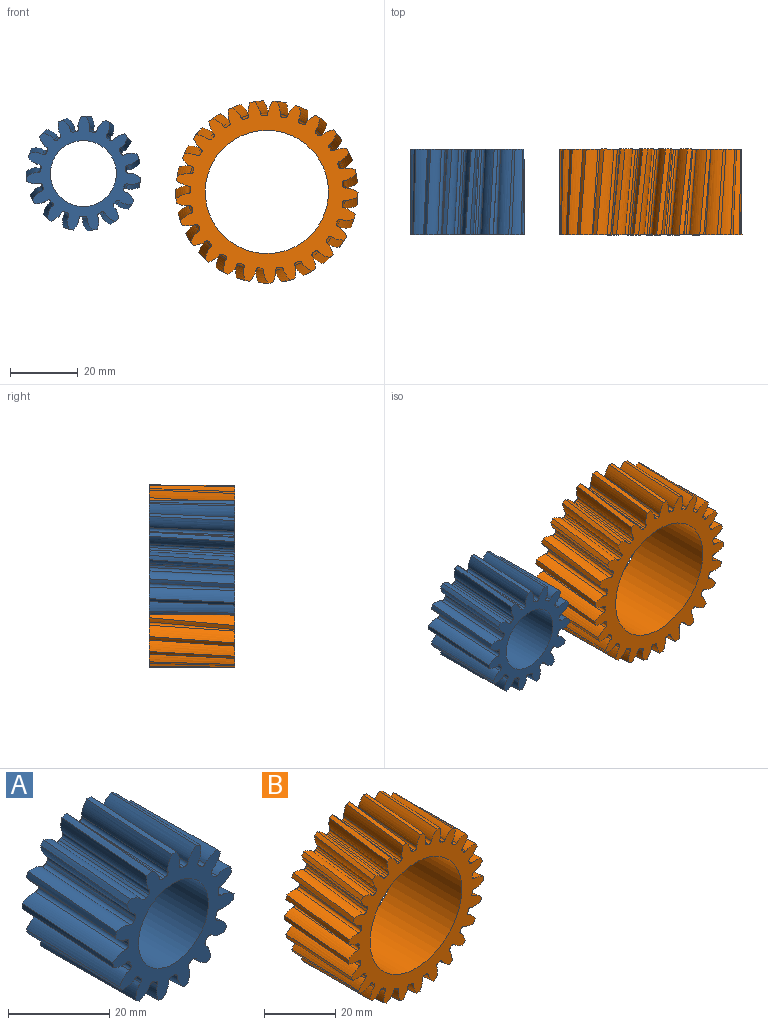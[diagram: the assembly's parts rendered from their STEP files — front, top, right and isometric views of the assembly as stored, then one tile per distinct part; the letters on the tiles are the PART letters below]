
ASSEMBLY  parts=2 mates=1
PART A: 93 faces, bbox 34.1x40.7x34 mm
  f0: bspline ~40.64x3.67mm, area 33.3mm2, adj f1,f89,f90,f91
  f1: bspline ~40.64x4.83mm, area 99.2mm2, adj f0,f2,f90,f91
  f2: bspline ~40.64x2.21mm, area 31.7mm2, adj f1,f3,f90,f91
  f3: bspline ~40.64x2.21mm, area 18mm2, adj f2,f4,f90,f91
  f4: bspline ~40.64x2.73mm, area 31.7mm2, adj f3,f5,f90,f91
  f5: bspline ~40.64x5.08mm, area 99.2mm2, adj f4,f6,f90,f91
  f6: bspline ~40.64x2.88mm, area 33.3mm2, adj f5,f7,f90,f91
  f7: bspline ~40.64x5.06mm, area 99.2mm2, adj f6,f8,f90,f91
  f8: bspline ~40.64x2.78mm, area 31.7mm2, adj f7,f9,f90,f91
  f9: bspline ~40.64x2.29mm, area 18mm2, adj f8,f10,f90,f91
  f10: bspline ~40.64x2.3mm, area 31.7mm2, adj f9,f11,f90,f91
  f11: bspline ~40.64x4.74mm, area 99.2mm2, adj f10,f12,f90,f91
  f12: bspline ~40.64x3.74mm, area 33.3mm2, adj f11,f13,f90,f91
  f13: bspline ~40.64x4.41mm, area 99.2mm2, adj f12,f14,f90,f91
  f14: bspline ~40.64x2.94mm, area 31.7mm2, adj f13,f15,f90,f91
  f15: bspline ~40.64x2.66mm, area 18mm2, adj f14,f16,f90,f91
  f16: bspline ~40.64x2.77mm, area 31.7mm2, adj f15,f17,f90,f91
  f17: bspline ~40.64x3.73mm, area 99.2mm2, adj f16,f18,f90,f91
  f18: bspline ~40.64x3.96mm, area 33.3mm2, adj f17,f19,f90,f91
  f19: bspline ~40.64x4.1mm, area 99.2mm2, adj f18,f20,f90,f91
  f20: bspline ~40.64x2.64mm, area 31.7mm2, adj f19,f21,f90,f91
  f21: bspline ~40.64x2.57mm, area 18mm2, adj f20,f22,f90,f91
  f22: bspline ~40.64x2.94mm, area 31.7mm2, adj f21,f23,f90,f91
  f23: bspline ~40.64x4.75mm, area 99.2mm2, adj f22,f24,f90,f91
  f24: bspline ~40.64x3.49mm, area 33.3mm2, adj f23,f25,f90,f91
  f25: bspline ~40.64x4.97mm, area 99.2mm2, adj f24,f26,f90,f91
  f26: bspline ~40.64x2.35mm, area 31.7mm2, adj f25,f27,f90,f91
  f27: bspline ~40.64x2.04mm, area 18mm2, adj f26,f28,f90,f91
  f28: bspline ~40.64x2.6mm, area 31.7mm2, adj f27,f29,f90,f91
  f29: bspline ~40.64x5.07mm, area 99.2mm2, adj f28,f30,f90,f91
  f30: bspline ~25.4x2.31mm, area 33.3mm2, adj f29,f31,f90,f91
  f31: bspline ~40.64x4.98mm, area 99.2mm2, adj f30,f32,f90,f91
  f32: bspline ~40.64x2.87mm, area 31.7mm2, adj f31,f33,f90,f91
  f33: bspline ~40.64x2.42mm, area 18mm2, adj f32,f34,f90,f91
  f34: bspline ~40.64x2.45mm, area 31.7mm2, adj f33,f35,f90,f91
  f35: bspline ~40.64x4.52mm, area 99.2mm2, adj f34,f36,f90,f91
  f36: bspline ~40.64x3.86mm, area 33.3mm2, adj f35,f37,f90,f91
  f37: bspline ~40.64x4.13mm, area 99.2mm2, adj f36,f38,f90,f91
  f38: bspline ~40.64x2.89mm, area 31.7mm2, adj f37,f39,f90,f91
  f39: bspline ~40.64x2.68mm, area 18mm2, adj f38,f40,f90,f91
  f40: bspline ~40.64x2.86mm, area 31.7mm2, adj f39,f41,f90,f91
  f41: bspline ~40.64x3.98mm, area 99.2mm2, adj f40,f42,f90,f91
  f42: bspline ~40.64x3.91mm, area 33.3mm2, adj f41,f43,f90,f91
  f43: bspline ~40.64x4.39mm, area 99.2mm2, adj f42,f44,f90,f91
  f44: bspline ~40.64x2.52mm, area 31.7mm2, adj f43,f45,f90,f91
  f45: bspline ~40.64x2.48mm, area 18mm2, adj f44,f46,f90,f91
  f46: bspline ~40.64x2.9mm, area 31.7mm2, adj f45,f47,f90,f91
  f47: bspline ~40.64x4.92mm, area 99.2mm2, adj f46,f48,f90,f91
  f48: bspline ~40.64x3.27mm, area 33.3mm2, adj f47,f49,f90,f91
  f49: bspline ~40.64x5.05mm, area 99.2mm2, adj f48,f50,f90,f91
  f50: bspline ~40.64x2.52mm, area 31.7mm2, adj f49,f51,f90,f91
  f51: bspline ~40.64x1.95mm, area 18mm2, adj f50,f52,f90,f91
  f52: bspline ~40.64x2.44mm, area 31.7mm2, adj f51,f53,f90,f91
  f53: bspline ~40.64x5.02mm, area 99.2mm2, adj f52,f54,f90,f91
  f54: bspline ~40.64x3.39mm, area 33.3mm2, adj f53,f55,f90,f91
  f55: bspline ~40.64x4.84mm, area 99.2mm2, adj f54,f56,f90,f91
  f56: bspline ~40.64x2.92mm, area 31.7mm2, adj f55,f57,f90,f91
  f57: bspline ~40.64x2.53mm, area 18mm2, adj f56,f58,f90,f91
  f58: bspline ~40.64x2.58mm, area 31.7mm2, adj f57,f59,f90,f91
  f59: bspline ~40.64x4.25mm, area 99.2mm2, adj f58,f60,f90,f91
  f60: bspline ~40.64x3.94mm, area 33.3mm2, adj f59,f61,f90,f91
  f61: bspline ~40.64x3.84mm, area 99.2mm2, adj f60,f62,f90,f91
  f62: bspline ~40.64x2.82mm, area 31.7mm2, adj f61,f63,f90,f91
  f63: bspline ~40.64x2.67mm, area 18mm2, adj f62,f64,f90,f91
  f64: bspline ~40.64x2.92mm, area 31.7mm2, adj f63,f65,f90,f91
  f65: bspline ~40.64x4.28mm, area 99.2mm2, adj f64,f66,f90,f91
  f66: bspline ~40.64x3.81mm, area 33.3mm2, adj f65,f67,f90,f91
  f67: bspline ~40.64x4.63mm, area 99.2mm2, adj f66,f68,f90,f91
  f68: bspline ~40.64x2.38mm, area 31.7mm2, adj f67,f69,f90,f91
  f69: bspline ~40.64x2.36mm, area 18mm2, adj f68,f70,f90,f91
  f70: bspline ~40.64x2.83mm, area 31.7mm2, adj f69,f71,f90,f91
  f71: bspline ~40.64x5.02mm, area 99.2mm2, adj f70,f72,f90,f91
  f72: bspline ~40.64x3.02mm, area 33.3mm2, adj f71,f73,f90,f91
  f73: bspline ~40.64x5.08mm, area 99.2mm2, adj f72,f74,f90,f91
  f74: bspline ~40.64x2.67mm, area 31.7mm2, adj f73,f75,f90,f91
  f75: bspline ~40.64x2.13mm, area 18mm2, adj f74,f76,f90,f91
  f76: bspline ~40.64x2.25mm, area 31.7mm2, adj f75,f77,f90,f91
  f77: bspline ~40.64x4.9mm, area 99.2mm2, adj f76,f78,f90,f91
  f78: bspline ~40.64x3.58mm, area 33.3mm2, adj f77,f79,f90,f91
  f79: bspline ~40.64x4.65mm, area 99.2mm2, adj f78,f80,f90,f91
  f80: bspline ~40.64x2.95mm, area 31.7mm2, adj f79,f81,f90,f91
  f81: bspline ~40.64x2.61mm, area 18mm2, adj f80,f82,f90,f91
  f82: bspline ~40.64x2.68mm, area 31.7mm2, adj f81,f83,f90,f91
  f83: bspline ~40.64x3.95mm, area 99.2mm2, adj f82,f84,f90,f91
  f84: bspline ~40.64x3.97mm, area 33.3mm2, adj f83,f85,f90,f91
  f85: bspline ~40.64x3.85mm, area 99.2mm2, adj f84,f86,f90,f91
  f86: bspline ~40.64x2.72mm, area 31.7mm2, adj f85,f87,f90,f91
  f87: bspline ~40.64x2.64mm, area 18mm2, adj f86,f88,f90,f91
  f88: bspline ~40.64x2.95mm, area 31.7mm2, adj f87,f89,f90,f91
  f89: bspline ~40.64x4.54mm, area 99.2mm2, adj f0,f88,f90,f91
  f90: plane 33.95x33.78mm, normal (0,1,0), area 389.3mm2, adj f0,f1,f2,f3,f4,f5,f6,f7
  f91: plane 33.95x33.8mm, normal (0,-1,0), area 389.7mm2, adj f0,f1,f2,f3,f4,f5,f6,f7
  f92: cylinder r=9.78mm len=25.4mm, axis (0,-1,0), area 1560.7mm2, adj f90,f91
PART B: 153 faces, bbox 54.1x40.7x54.1 mm
  f0: bspline ~40.64x4.19mm, area 36.5mm2, adj f1,f149,f150,f151
  f1: bspline ~40.64x6.35mm, area 99.8mm2, adj f0,f2,f150,f151
  f2: bspline ~40.64x3.93mm, area 29.9mm2, adj f1,f3,f150,f151
  f3: bspline ~40.64x3.45mm, area 17.2mm2, adj f2,f4,f150,f151
  f4: bspline ~40.64x3.43mm, area 29.9mm2, adj f3,f5,f150,f151
  f5: bspline ~40.64x5.8mm, area 99.8mm2, adj f4,f6,f150,f151
  f6: bspline ~40.64x5.01mm, area 36.5mm2, adj f5,f7,f150,f151
  f7: bspline ~40.64x6.28mm, area 99.8mm2, adj f6,f8,f150,f151
  f8: bspline ~40.64x4.31mm, area 29.9mm2, adj f7,f9,f150,f151
  f9: bspline ~40.64x3.95mm, area 17.2mm2, adj f8,f10,f150,f151
  f10: bspline ~40.64x3.98mm, area 29.9mm2, adj f9,f11,f150,f151
  f11: bspline ~40.64x4.97mm, area 99.8mm2, adj f10,f12,f150,f151
  f12: bspline ~40.64x5.51mm, area 36.5mm2, adj f11,f13,f150,f151
  f13: bspline ~40.64x5.81mm, area 99.8mm2, adj f12,f14,f150,f151
  f14: bspline ~40.64x4.42mm, area 29.9mm2, adj f13,f15,f150,f151
  f15: bspline ~40.64x4.2mm, area 17.2mm2, adj f14,f16,f150,f151
  f16: bspline ~40.64x4.29mm, area 29.9mm2, adj f15,f17,f150,f151
  f17: bspline ~40.64x5.13mm, area 99.8mm2, adj f16,f18,f150,f151
  f18: bspline ~40.64x5.67mm, area 36.5mm2, adj f17,f19,f150,f151
  f19: bspline ~40.64x5.02mm, area 99.8mm2, adj f18,f20,f150,f151
  f20: bspline ~40.64x4.25mm, area 29.9mm2, adj f19,f21,f150,f151
  f21: bspline ~40.64x4.18mm, area 17.2mm2, adj f20,f22,f150,f151
  f22: bspline ~40.64x4.42mm, area 29.9mm2, adj f21,f23,f150,f151
  f23: bspline ~40.64x5.89mm, area 99.8mm2, adj f22,f24,f150,f151
  f24: bspline ~40.64x5.47mm, area 36.5mm2, adj f23,f25,f150,f151
  f25: bspline ~40.64x5.09mm, area 99.8mm2, adj f24,f26,f150,f151
  f26: bspline ~40.64x3.92mm, area 29.9mm2, adj f25,f27,f150,f151
  f27: bspline ~40.64x3.9mm, area 17.2mm2, adj f26,f28,f150,f151
  f28: bspline ~40.64x4.28mm, area 29.9mm2, adj f27,f29,f150,f151
  f29: bspline ~40.64x6.31mm, area 99.8mm2, adj f28,f30,f150,f151
  f30: bspline ~40.64x4.92mm, area 36.5mm2, adj f29,f31,f150,f151
  f31: bspline ~40.64x5.88mm, area 99.8mm2, adj f30,f32,f150,f151
  f32: bspline ~40.64x3.35mm, area 29.9mm2, adj f31,f33,f150,f151
  f33: bspline ~40.64x3.38mm, area 17.2mm2, adj f32,f34,f150,f151
  f34: bspline ~40.64x3.87mm, area 29.9mm2, adj f33,f35,f150,f151
  f35: bspline ~40.64x6.33mm, area 99.8mm2, adj f34,f36,f150,f151
  f36: bspline ~40.64x4.07mm, area 36.5mm2, adj f35,f37,f150,f151
  f37: bspline ~40.64x6.3mm, area 99.8mm2, adj f36,f38,f150,f151
  f38: bspline ~40.64x3.8mm, area 29.9mm2, adj f37,f39,f150,f151
  f39: bspline ~40.64x3.3mm, area 17.2mm2, adj f38,f40,f150,f151
  f40: bspline ~40.64x3.26mm, area 29.9mm2, adj f39,f41,f150,f151
  f41: bspline ~40.64x5.96mm, area 99.8mm2, adj f40,f42,f150,f151
  f42: bspline ~40.64x4.83mm, area 36.5mm2, adj f41,f43,f150,f151
  f43: bspline ~40.64x6.33mm, area 99.8mm2, adj f42,f44,f150,f151
  f44: bspline ~40.64x4.24mm, area 29.9mm2, adj f43,f45,f150,f151
  f45: bspline ~40.64x3.85mm, area 17.2mm2, adj f44,f46,f150,f151
  f46: bspline ~40.64x3.87mm, area 29.9mm2, adj f45,f47,f150,f151
  f47: bspline ~40.64x5.21mm, area 99.8mm2, adj f46,f48,f150,f151
  f48: bspline ~40.64x5.42mm, area 36.5mm2, adj f47,f49,f150,f151
  f49: bspline ~40.64x5.96mm, area 99.8mm2, adj f48,f50,f150,f151
  f50: bspline ~40.64x4.42mm, area 29.9mm2, adj f49,f51,f150,f151
  f51: bspline ~40.64x4.16mm, area 17.2mm2, adj f50,f52,f150,f151
  f52: bspline ~40.64x4.23mm, area 29.9mm2, adj f51,f53,f150,f151
  f53: bspline ~40.64x4.91mm, area 99.8mm2, adj f52,f54,f150,f151
  f54: bspline ~40.64x5.66mm, area 36.5mm2, adj f53,f55,f150,f151
  f55: bspline ~40.64x5.23mm, area 99.8mm2, adj f54,f56,f150,f151
  f56: bspline ~40.64x4.32mm, area 29.9mm2, adj f55,f57,f150,f151
  f57: bspline ~40.64x4.21mm, area 17.2mm2, adj f56,f58,f150,f151
  f58: bspline ~40.64x4.41mm, area 29.9mm2, adj f57,f59,f150,f151
  f59: bspline ~40.64x5.72mm, area 99.8mm2, adj f58,f60,f150,f151
  f60: bspline ~40.64x5.55mm, area 36.5mm2, adj f59,f61,f150,f151
  f61: bspline ~40.64x4.84mm, area 99.8mm2, adj f60,f62,f150,f151
  f62: bspline ~40.64x4.03mm, area 29.9mm2, adj f61,f63,f150,f151
  f63: bspline ~40.64x3.99mm, area 17.2mm2, adj f62,f64,f150,f151
  f64: bspline ~40.64x4.34mm, area 29.9mm2, adj f63,f65,f150,f151
  f65: bspline ~40.64x6.24mm, area 99.8mm2, adj f64,f66,f150,f151
  f66: bspline ~40.64x5.09mm, area 36.5mm2, adj f65,f67,f150,f151
  f67: bspline ~40.64x5.72mm, area 99.8mm2, adj f66,f68,f150,f151
  f68: bspline ~40.64x3.51mm, area 29.9mm2, adj f67,f69,f150,f151
  f69: bspline ~40.64x3.53mm, area 17.2mm2, adj f68,f70,f150,f151
  f70: bspline ~40.64x3.99mm, area 29.9mm2, adj f69,f71,f150,f151
  f71: bspline ~40.64x6.36mm, area 99.8mm2, adj f70,f72,f150,f151
  f72: bspline ~40.64x4.31mm, area 36.5mm2, adj f71,f73,f150,f151
  f73: bspline ~40.64x6.24mm, area 99.8mm2, adj f72,f74,f150,f151
  f74: bspline ~40.64x3.65mm, area 29.9mm2, adj f73,f75,f150,f151
  f75: bspline ~40.64x3.12mm, area 17.2mm2, adj f74,f76,f150,f151
  f76: bspline ~40.64x3.4mm, area 29.9mm2, adj f75,f77,f150,f151
  f77: bspline ~40.64x6.09mm, area 99.8mm2, adj f76,f78,f150,f151
  f78: bspline ~40.64x4.64mm, area 36.5mm2, adj f77,f79,f150,f151
  f79: bspline ~40.64x6.36mm, area 99.8mm2, adj f78,f80,f150,f151
  f80: bspline ~40.64x4.16mm, area 29.9mm2, adj f79,f81,f150,f151
  f81: bspline ~40.64x3.73mm, area 17.2mm2, adj f80,f82,f150,f151
  f82: bspline ~40.64x3.74mm, area 29.9mm2, adj f81,f83,f150,f151
  f83: bspline ~40.64x5.43mm, area 99.8mm2, adj f82,f84,f150,f151
  f84: bspline ~40.64x5.3mm, area 36.5mm2, adj f83,f85,f150,f151
  f85: bspline ~40.64x6.09mm, area 99.8mm2, adj f84,f86,f150,f151
  f86: bspline ~40.64x4.4mm, area 29.9mm2, adj f85,f87,f150,f151
  f87: bspline ~40.64x4.11mm, area 17.2mm2, adj f86,f88,f150,f151
  f88: bspline ~40.64x4.16mm, area 29.9mm2, adj f87,f89,f150,f151
  f89: bspline ~40.64x4.69mm, area 99.8mm2, adj f88,f90,f150,f151
  f90: bspline ~40.64x5.63mm, area 36.5mm2, adj f89,f91,f150,f151
  f91: bspline ~40.64x5.44mm, area 99.8mm2, adj f90,f92,f150,f151
  f92: bspline ~40.64x4.37mm, area 29.9mm2, adj f91,f93,f150,f151
  f93: bspline ~40.64x4.22mm, area 17.2mm2, adj f92,f94,f150,f151
  f94: bspline ~40.64x4.39mm, area 29.9mm2, adj f93,f95,f150,f151
  f95: bspline ~40.64x5.54mm, area 99.8mm2, adj f94,f96,f150,f151
  f96: bspline ~40.64x5.61mm, area 36.5mm2, adj f95,f97,f150,f151
  f97: bspline ~40.64x4.58mm, area 99.8mm2, adj f96,f98,f150,f151
  f98: bspline ~40.64x4.12mm, area 29.9mm2, adj f97,f99,f150,f151
  f99: bspline ~40.64x4.07mm, area 17.2mm2, adj f98,f100,f150,f151
  f100: bspline ~40.64x4.38mm, area 29.9mm2, adj f99,f101,f150,f151
  f101: bspline ~40.64x6.15mm, area 99.8mm2, adj f100,f102,f150,f151
  f102: bspline ~40.64x5.24mm, area 36.5mm2, adj f101,f103,f150,f151
  f103: bspline ~40.64x5.53mm, area 99.8mm2, adj f102,f104,f150,f151
  f104: bspline ~40.64x3.67mm, area 29.9mm2, adj f103,f105,f150,f151
  f105: bspline ~40.64x3.67mm, area 17.2mm2, adj f104,f106,f150,f151
  f106: bspline ~40.64x4.11mm, area 29.9mm2, adj f105,f107,f150,f151
  f107: bspline ~40.64x6.37mm, area 99.8mm2, adj f106,f108,f150,f151
  f108: bspline ~40.64x4.53mm, area 36.5mm2, adj f107,f109,f150,f151
  f109: bspline ~40.64x6.14mm, area 99.8mm2, adj f108,f110,f150,f151
  f110: bspline ~40.64x3.49mm, area 29.9mm2, adj f109,f111,f150,f151
  f111: bspline ~40.64x3.03mm, area 17.2mm2, adj f110,f112,f150,f151
  f112: bspline ~40.64x3.57mm, area 29.9mm2, adj f111,f113,f150,f151
  f113: bspline ~40.64x6.19mm, area 99.8mm2, adj f112,f114,f150,f151
  f114: bspline ~40.64x4.42mm, area 36.5mm2, adj f113,f115,f150,f151
  f115: bspline ~40.64x6.37mm, area 99.8mm2, adj f114,f116,f150,f151
  f116: bspline ~40.64x4.05mm, area 29.9mm2, adj f115,f117,f150,f151
  f117: bspline ~40.64x3.6mm, area 17.2mm2, adj f116,f118,f150,f151
  f118: bspline ~40.64x3.59mm, area 29.9mm2, adj f117,f119,f150,f151
  f119: bspline ~40.64x5.63mm, area 99.8mm2, adj f118,f120,f150,f151
  f120: bspline ~40.64x5.17mm, area 36.5mm2, adj f119,f121,f150,f151
  f121: bspline ~40.64x6.2mm, area 99.8mm2, adj f120,f122,f150,f151
  f122: bspline ~40.64x4.36mm, area 29.9mm2, adj f121,f123,f150,f151
  f123: bspline ~40.64x4.04mm, area 17.2mm2, adj f122,f124,f150,f151
  f124: bspline ~40.64x4.08mm, area 29.9mm2, adj f123,f125,f150,f151
  f125: bspline ~40.64x4.71mm, area 99.8mm2, adj f124,f126,f150,f151
  f126: bspline ~40.64x5.58mm, area 36.5mm2, adj f125,f127,f150,f151
  f127: bspline ~40.64x5.63mm, area 99.8mm2, adj f126,f128,f150,f151
  f128: bspline ~40.64x4.4mm, area 29.9mm2, adj f127,f129,f150,f151
  f129: bspline ~40.64x4.22mm, area 17.2mm2, adj f128,f130,f150,f151
  f130: bspline ~40.64x4.35mm, area 29.9mm2, adj f129,f131,f150,f151
  f131: bspline ~40.64x5.34mm, area 99.8mm2, adj f130,f132,f150,f151
  f132: bspline ~40.64x5.65mm, area 36.5mm2, adj f131,f133,f150,f151
  f133: bspline ~40.64x4.8mm, area 99.8mm2, adj f132,f134,f150,f151
  f134: bspline ~40.64x4.2mm, area 29.9mm2, adj f133,f135,f150,f151
  f135: bspline ~40.64x4.13mm, area 17.2mm2, adj f134,f136,f150,f151
  f136: bspline ~40.64x4.41mm, area 29.9mm2, adj f135,f137,f150,f151
  f137: bspline ~40.64x6.03mm, area 99.8mm2, adj f136,f138,f150,f151
  f138: bspline ~40.64x5.36mm, area 36.5mm2, adj f137,f139,f150,f151
  f139: bspline ~40.64x5.32mm, area 99.8mm2, adj f138,f140,f150,f151
  f140: bspline ~40.64x3.8mm, area 29.9mm2, adj f139,f141,f150,f151
  f141: bspline ~40.64x3.79mm, area 17.2mm2, adj f140,f142,f150,f151
  f142: bspline ~40.64x4.2mm, area 29.9mm2, adj f141,f143,f150,f151
  f143: bspline ~40.64x6.35mm, area 99.8mm2, adj f142,f144,f150,f151
  f144: bspline ~40.64x4.74mm, area 36.5mm2, adj f143,f145,f150,f151
  f145: bspline ~40.64x6.02mm, area 99.8mm2, adj f144,f146,f150,f151
  f146: bspline ~40.64x3.31mm, area 29.9mm2, adj f145,f147,f150,f151
  f147: bspline ~40.64x3.21mm, area 17.2mm2, adj f146,f148,f150,f151
  f148: bspline ~40.64x3.73mm, area 29.9mm2, adj f147,f149,f150,f151
  f149: bspline ~40.64x6.27mm, area 99.8mm2, adj f0,f148,f150,f151
  f150: plane 53.99x53.89mm, normal (0,1,0), area 892.9mm2, adj f0,f1,f2,f3,f4,f5,f6,f7
  f151: plane 53.97x53.95mm, normal (0,-1,0), area 893.1mm2, adj f0,f1,f2,f3,f4,f5,f6,f7
  f152: cylinder r=18.26mm len=36.51mm, axis (0,-1,0), area 2913.6mm2, adj f150,f151
PLACE A t=(-54.43,12.86,5.59)mm
PLACE B t=(-0.07,12.86,0.14)mm
MATE fastened A.f90 <-> B.f150  axis (0,1,0) through (-43.07,12.86,0.14)mm
